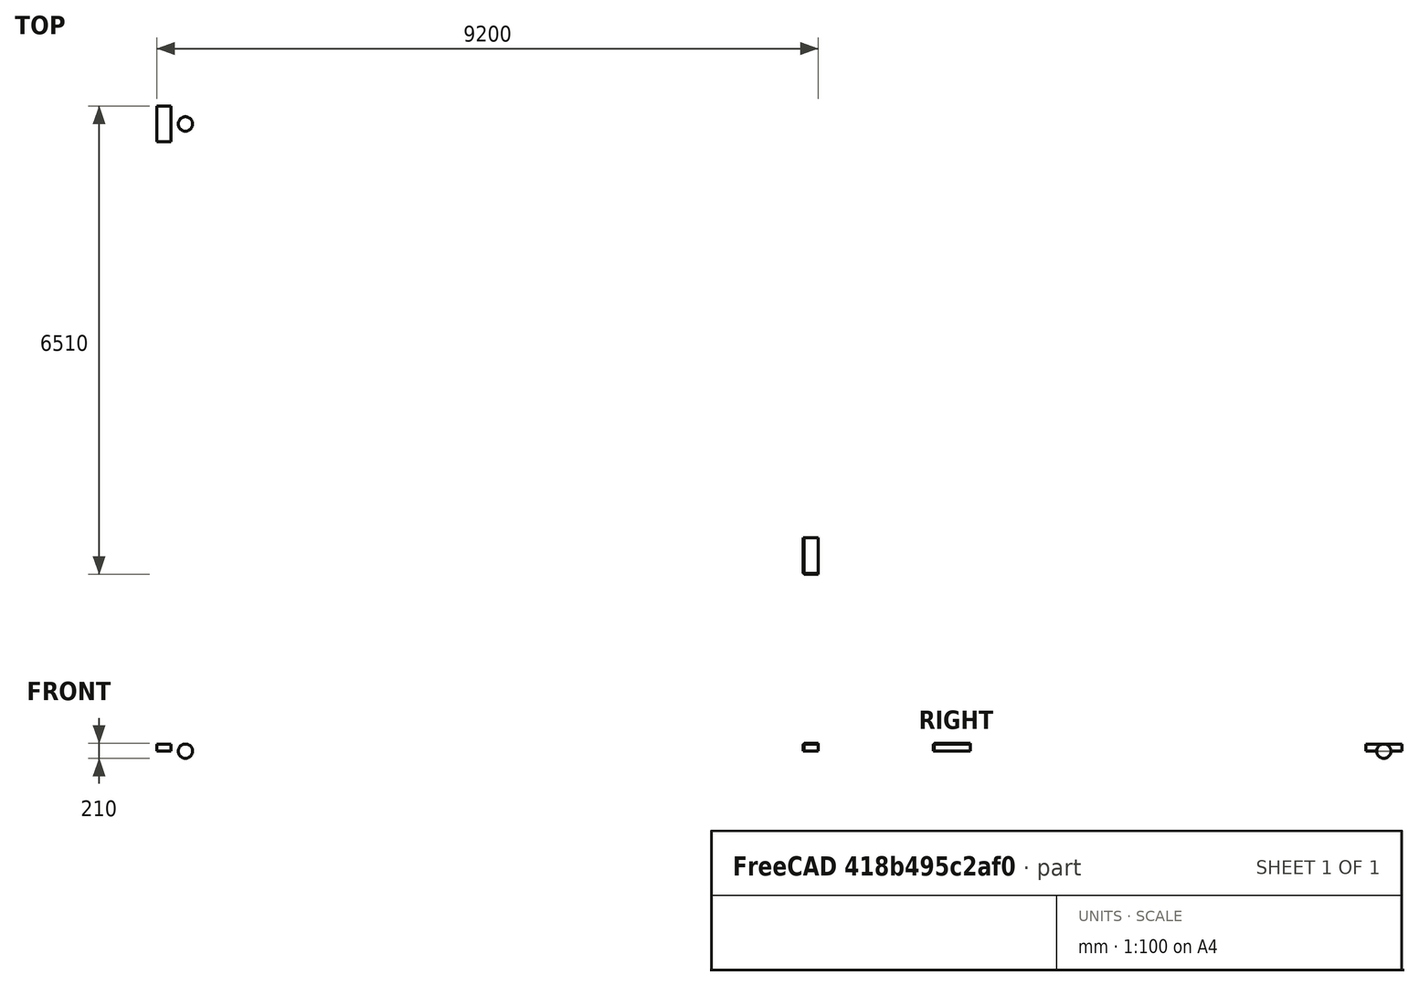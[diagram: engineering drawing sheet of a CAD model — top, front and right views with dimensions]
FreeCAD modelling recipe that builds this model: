
FCSTD DOCUMENT  (FreeCAD 0.20R28671 (Git))
Label: draft_test_objects
License: Creative Commons Attribution
LicenseURL: http://creativecommons.org/licenses/by/4.0/
objects: Part::Part2DObjectPython×39, App::Annotation×37, Part::FeaturePython×21, App::FeaturePython×9, Part::Box×3, Part::Feature×1, Part::Mirroring×1, Part::Sphere×1, App::DocumentObjectGroupPython×1
note: 62 computed .brp shape members not serialized (recipe doc carries the construction recipe); baked Part::Feature solids carry a one-line shape summary decoded from their .brp

FEATURE [App::Annotation] Description
  LabelText = Draft test file | Created: 2022/04/14T09:40:22 | Version: 0.20.28671 (Git) | Release: Unknown 2022/04/09 23:07:02 | Branch: 
  Position = (0,-1000,0)
FEATURE [Part::Feature] Frame
  shape: bbox 18000 x 12000 x 2e-07 mm, 0 faces, 0 solids (baked)
FEATURE [Part::Part2DObjectPython] Line  # Draft 2D object (typed FeaturePython)
  Area = 0
  ChamferSize = 0
  Closed = false
  End = (500,500,0)
  FilletRadius = 0
  Length = 707.107
  MakeFace = true
  Points = (2) [(0,0,0),(500,500,0)]
  Start = (0,0,0)
  Subdivisions = 0
FEATURE [App::Annotation] Annotation
  LabelText = Line
  Position = (0,-200,0)
FEATURE [Part::Part2DObjectPython] Wire  # Draft 2D object (typed FeaturePython)
  Area = 0
  ChamferSize = 0
  Closed = false
  End = (1500,500,0)
  FilletRadius = 0
  Length = 809.017
  MakeFace = true
  Points = (3) [(1000,0,0),(1500,250,0),(1500,500,0)]
  Start = (1000,0,0)
  Subdivisions = 0
FEATURE [App::Annotation] Annotation001
  LabelText = Wire
  Position = (1000,-200,0)
FEATURE [Part::Part2DObjectPython] Line001  # Draft 2D object (typed FeaturePython)
  Area = 0
  ChamferSize = 0
  Closed = false
  End = (2000,500,0)
  FilletRadius = 0
  Length = 500
  MakeFace = true
  Points = (2) [(2000,0,0),(2000,500,0)]
  Start = (2000,0,0)
  Subdivisions = 0
FEATURE [Part::Part2DObjectPython] Line002  # Draft 2D object (typed FeaturePython)
  Area = 0
  ChamferSize = 0
  Closed = false
  End = (2500,500,0)
  FilletRadius = 0
  Length = 500
  MakeFace = true
  Points = (2) [(2000,500,0),(2500,500,0)]
  Start = (2000,500,0)
  Subdivisions = 0
FEATURE [Part::Part2DObjectPython] Fillet  # Draft 2D object (typed FeaturePython)
  End = (2500,500,0)
  FilletRadius = 400
  Length = 828.319
  Start = (2000,0,0)
FEATURE [App::Annotation] Annotation002
  LabelText = Fillet
  Position = (2000,-200,0)
FEATURE [Part::Part2DObjectPython] Arc  # Draft 2D object (typed FeaturePython)
  Area = 0
  FirstAngle = 90
  LastAngle = 270
  MakeFace = true
  Placement = pos=(3250,250,0) rot=(0,0,1;0rad)
  Radius = 250
FEATURE [App::Annotation] Annotation003
  LabelText = Circular arc
  Position = (3000,-200,0)
FEATURE [Part::Part2DObjectPython] Arc001  # Draft 2D object (typed FeaturePython)
  Area = 0
  FirstAngle = 0
  LastAngle = 180
  MakeFace = false
  Placement = pos=(4250,250,0) rot=(0.707107,-0.707107,0;3.14159rad)
  Radius = 250
FEATURE [App::Annotation] Annotation004
  LabelText = Circular arc 3 points
  Position = (4000,-200,0)
FEATURE [Part::Part2DObjectPython] Circle  # Draft 2D object (typed FeaturePython)
  Area = 196350
  FirstAngle = 0
  LastAngle = 0
  MakeFace = true
  Placement = pos=(5250,250,0) rot=(0,0,1;0rad)
  Radius = 250
FEATURE [App::Annotation] Annotation005
  LabelText = Circle
  Position = (5000,-200,0)
FEATURE [Part::Part2DObjectPython] Ellipse  # Draft 2D object (typed FeaturePython)
  Area = 117810
  FirstAngle = 0
  LastAngle = 0
  MajorRadius = 250
  MakeFace = true
  MinorRadius = 150
  Placement = pos=(6250,150,0) rot=(0,0,1;0rad)
FEATURE [App::Annotation] Annotation006
  LabelText = Ellipse
  Position = (6000,-200,0)
FEATURE [Part::Part2DObjectPython] Rectangle  # Draft 2D object (typed FeaturePython)
  Area = 150000
  ChamferSize = 0
  Columns = 1
  FilletRadius = 0
  Height = 300
  Length = 500
  MakeFace = true
  Placement = pos=(7000,0,0) rot=(0,0,1;0rad)
  Rows = 1
FEATURE [App::Annotation] Annotation007
  LabelText = Rectangle
  Position = (7000,-200,0)
FEATURE [Part::Part2DObjectPython] Polygon  # Draft 2D object (typed FeaturePython)
  Area = 148603
  ChamferSize = 0
  DrawMode = 0
  FacesNumber = 5
  FilletRadius = 0
  MakeFace = true
  Placement = pos=(8250,250,0) rot=(0,0,1;0rad)
  Radius = 250
FEATURE [App::Annotation] Annotation008
  LabelText = Polygon
  Position = (8000,-200,0)
FEATURE [Part::Part2DObjectPython] BSpline  # Draft 2D object (typed FeaturePython)
  Area = 0
  Closed = false
  MakeFace = true
  Parameterization = 1
  Points = (4) [(9000,0,0),(9100,200,0),(9400,300,0),(9500,500,0)]
FEATURE [App::Annotation] Annotation009
  LabelText = BSpline
  Position = (9000,-200,0)
FEATURE [Part::Part2DObjectPython] BezCurve  # Draft 2D object (typed FeaturePython)
  Area = 0
  Closed = false
  Degree = 3
  Length = 838.374
  MakeFace = true
  Points = (4) [(10000,0,0),(10000,500,0),(10500,0,0),(10500,500,0)]
FEATURE [App::Annotation] Annotation010
  LabelText = Cubic bezier
  Position = (10000,-200,0)
FEATURE [Part::Part2DObjectPython] BezCurve001  # Draft 2D object (typed FeaturePython)
  Area = 0
  Closed = false
  Degree = 4
  Length = 800.125
  MakeFace = true
  Points = (5) [(11000,0,0),(11100,400,0),(11250,250,0),(11400,100,0),(11500,500,0)]
FEATURE [App::Annotation] Annotation011
  LabelText = N-degree bezier
  Position = (11000,-200,0)
FEATURE [Part::FeaturePython] Point  # WARN: FeaturePython — macro-defined, semantics opaque (R4)
  Placement = pos=(12000,0,0) rot=(0,0,1;0rad)
  X = 12000
  Y = 0
  Z = 0
FEATURE [App::Annotation] Annotation012
  LabelText = Point
  Position = (12000,-200,0)
FEATURE [Part::Box] Box
  AttacherType = Attacher::AttachEngine3D
  Height = 100
  Length = 200
  Placement = pos=(13000,0,0) rot=(0,0,1;0rad)
  Width = 500
FEATURE [Part::FeaturePython] Facebinder  # WARN: FeaturePython — macro-defined, semantics opaque (R4)
  Area = 170000
  Extrusion = 10
  Faces = -> [Box]
  RemoveSplitter = false
  Sew = false
FEATURE [App::Annotation] Annotation013
  LabelText = Facebinder
  Position = (13000,-200,0)
FEATURE [Part::Part2DObjectPython] ShapeString  # Draft 2D object (typed FeaturePython)
  FontFile = <path>
  MakeFace = true
  Placement = pos=(14000,0,0) rot=(0,0,1;0rad)
  Size = 100
  String = Testing
  Tracking = 0
FEATURE [App::Annotation] Annotation014
  LabelText = Shapestring
  Position = (14000,-200,0)
FEATURE [Part::Part2DObjectPython] Rectangle001  # Draft 2D object (typed FeaturePython)
  Area = 150000
  ChamferSize = 0
  Columns = 1
  FilletRadius = 0
  Height = 300
  Length = 500
  MakeFace = true
  Placement = pos=(15000,0,0) rot=(0,0,1;0rad)
  Rows = 1
FEATURE [Part::FeaturePython] Hatch  # WARN: FeaturePython — macro-defined, semantics opaque (R4)
  Base = -> Rectangle001
  File = <path>
  Pattern = Horizontal5
  Rotation = 45
  Scale = 10
  Translate = true
FEATURE [App::Annotation] Annotation015
  LabelText = Hatch
  Position = (15000,-200,0)
FEATURE [App::FeaturePython] Text  # WARN: FeaturePython — macro-defined, semantics opaque (R4)
  Placement = pos=(0,2100,0) rot=(0,0,1;0rad)
  Text = Testing | text
FEATURE [App::Annotation] Annotation016
  LabelText = Text
  Position = (0,1800,0)
FEATURE [App::FeaturePython] Dimension  # Draft dimension (typed FeaturePython)
  Diameter = false
  Dimline = (1000,2200,0)
  Direction = (0,0,0)
  Distance = 400
  End = (1500,2400,0)
  Normal = (0,0,1)
  Start = (1500,2000,0)
FEATURE [Part::Part2DObjectPython] Line003  # Draft 2D object (typed FeaturePython)
  Area = 0
  ChamferSize = 0
  Closed = false
  End = (1500,3000,0)
  FilletRadius = 0
  Length = 400
  MakeFace = true
  Points = (2) [(1500,2600,0),(1500,3000,0)]
  Start = (1500,2600,0)
  Subdivisions = 0
FEATURE [App::FeaturePython] Dimension001  # Draft dimension (typed FeaturePython)
  Diameter = false
  Dimline = (1000,2800,0)
  Direction = (0,0,0)
  Distance = 400
  End = (1500,3000,0)
  LinkedGeometry = -> [Line003]
  Normal = (0,0,1)
  Start = (1500,2600,0)
  Support = -> Line003
FEATURE [App::Annotation] Annotation017
  LabelText = Dimension
  Position = (1000,1800,0)
FEATURE [Part::Part2DObjectPython] Circle001  # Draft 2D object (typed FeaturePython)
  Area = 0
  FirstAngle = 0
  LastAngle = 0
  MakeFace = false
  Placement = pos=(2200,2200,0) rot=(0,0,1;0rad)
  Radius = 200
FEATURE [App::FeaturePython] Dimension002  # Draft dimension (typed FeaturePython)
  Diameter = false
  Dimline = (2300,2300,0)
  Direction = (0,0,0)
  Distance = 200
  End = (2341.42,2341.42,0)
  LinkedGeometry = -> [Circle001]
  Normal = (0,0,1)
  Start = (2200,2200,0)
  Support = -> Circle001
FEATURE [Part::Part2DObjectPython] Circle002  # Draft 2D object (typed FeaturePython)
  Area = 0
  FirstAngle = 0
  LastAngle = 0
  MakeFace = false
  Placement = pos=(2200,2800,0) rot=(0,0,1;0rad)
  Radius = 200
FEATURE [App::FeaturePython] Dimension003  # Draft dimension (typed FeaturePython)
  Diameter = true
  Dimline = (2300,2900,0)
  Direction = (0,0,0)
  Distance = 400
  End = (2341.42,2941.42,0)
  LinkedGeometry = -> [Circle002]
  Normal = (0,0,1)
  Start = (2058.58,2658.58,0)
  Support = -> Circle002
FEATURE [App::Annotation] Annotation018
  LabelText = Radius dimension | Diameter dimension
  Position = (2000,1800,0)
FEATURE [Part::Part2DObjectPython] Line004  # Draft 2D object (typed FeaturePython)
  Area = 0
  ChamferSize = 0
  Closed = false
  End = (3500,2000,0)
  FilletRadius = 0
  Length = 500
  MakeFace = true
  Points = (2) [(3000,2000,0),(3500,2000,0)]
  Start = (3000,2000,0)
  Subdivisions = 0
FEATURE [Part::Part2DObjectPython] Line005  # Draft 2D object (typed FeaturePython)
  Area = 0
  ChamferSize = 0
  Closed = false
  End = (3500,2500,0)
  FilletRadius = 0
  Length = 707.107
  MakeFace = true
  Points = (2) [(3000,2000,0),(3500,2500,0)]
  Start = (3000,2000,0)
  Subdivisions = 0
FEATURE [App::FeaturePython] Dimension004  # Draft dimension (typed FeaturePython)
  Angle = 45
  Center = (3000,2000,0)
  Dimline = (3250,2250,0)
  FirstAngle = 0
  LastAngle = 45
  Normal = (0,0,1)
FEATURE [App::Annotation] Annotation019
  LabelText = Angle dimension
  Position = (3000,1800,0)
FEATURE [App::FeaturePython] dLabel  # WARN: FeaturePython — macro-defined, semantics opaque (R4)
  CustomText = Example label
  LabelType = 0
  Placement = pos=(4250,2250,0) rot=(0,0,1;0rad)
  Points = (3) [(4250,2250,0),(4150,2250,0),(4000,2000,0)]
  StraightDirection = 0
  StraightDistance = -100
  TargetPoint = (4000,2000,0)
  Text = Example label
FEATURE [App::Annotation] Annotation020
  LabelText = Label
  Position = (4000,1800,0)
FEATURE [Part::Part2DObjectPython] Rectangle002  # Draft 2D object (typed FeaturePython)
  Area = 5000
  ChamferSize = 0
  Columns = 1
  FilletRadius = 0
  Height = 50
  Length = 100
  MakeFace = true
  Placement = pos=(0,4000,0) rot=(0,0,1;0rad)
  Rows = 1
FEATURE [Part::FeaturePython] Array  # Draft array (typed FeaturePython)
  Angle = 360
  ArrayType = 0
  Axis = (0,0,1)
  Base = -> Rectangle002
  Center = (0,0,0)
  Fuse = false
  IntervalAxis = (0,0,0)
  IntervalX = (200,0,0)
  IntervalY = (0,150,0)
  IntervalZ = (0,0,0)
  NumberCircles = 3
  NumberPolar = 5
  NumberX = 3
  NumberY = 2
  NumberZ = 1
  RadialDistance = 50
  Symmetry = 1
  TangentialDistance = 25
FEATURE [App::Annotation] Annotation021
  LabelText = Orthogonal array
  Position = (0,3800,0)
FEATURE [Part::Part2DObjectPython] Rectangle003  # Draft 2D object (typed FeaturePython)
  Area = 2500
  ChamferSize = 0
  Columns = 1
  FilletRadius = 0
  Height = 50
  Length = 50
  MakeFace = true
  Placement = pos=(1000,4000,0) rot=(0,0,1;0rad)
  Rows = 1
FEATURE [Part::FeaturePython] Array001  # Draft array (typed FeaturePython)
  AlwaysSyncPlacement = false
  Angle = 360
  ArrayType = 0
  Axis = (0,0,1)
  Base = -> Rectangle003
  Center = (0,0,0)
  Count = 6
  ExpandArray = false
  Fuse = false
  IntervalAxis = (0,0,0)
  IntervalX = (200,0,0)
  IntervalY = (0,150,0)
  IntervalZ = (0,0,0)
  NumberCircles = 3
  NumberPolar = 5
  NumberX = 3
  NumberY = 2
  NumberZ = 1
  PlacementList = 6 placements: [(1000,4000,0),(1000,4150,0),(1200,4000,0),(1200,4150,0),(1400,4000,0),(1400,4150,0)]
  RadialDistance = 50
  ScaleList = (6) [(1,1,1),(1,1,1),(1,1,1),(1,1,1),(1,1,1),(1,1,1)]
  Symmetry = 1
  TangentialDistance = 25
FEATURE [App::Annotation] Annotation022
  LabelText = Orthogonal link array
  Position = (1000,3800,0)
FEATURE [Part::Part2DObjectPython] Wire001  # Draft 2D object (typed FeaturePython)
  Area = 0
  ChamferSize = 0
  Closed = false
  End = (2100,4000,0)
  FilletRadius = 0
  Length = 150
  MakeFace = true
  Points = (3) [(2000,4050,0),(2000,4000,0),(2100,4000,0)]
  Start = (2000,4050,0)
  Subdivisions = 0
FEATURE [Part::FeaturePython] Array002  # Draft array (typed FeaturePython)
  Angle = 90
  ArrayType = 1
  Axis = (0,0,1)
  Base = -> Wire001
  Center = (2000,4250,0)
  Fuse = false
  IntervalAxis = (0,0,0)
  IntervalX = (50,0,0)
  IntervalY = (0,50,0)
  IntervalZ = (0,0,50)
  NumberCircles = 3
  NumberPolar = 4
  NumberX = 2
  NumberY = 2
  NumberZ = 1
  RadialDistance = 50
  Symmetry = 1
  TangentialDistance = 25
FEATURE [App::Annotation] Annotation023
  LabelText = Polar array
  Position = (2000,3800,0)
FEATURE [Part::Part2DObjectPython] Wire002  # Draft 2D object (typed FeaturePython)
  Area = 0
  ChamferSize = 0
  Closed = false
  End = (3050,4000,0)
  FilletRadius = 0
  Length = 100
  MakeFace = true
  Points = (3) [(3000,4050,0),(3000,4000,0),(3050,4000,0)]
  Start = (3000,4050,0)
  Subdivisions = 0
FEATURE [Part::FeaturePython] Array003  # Draft array (typed FeaturePython)
  AlwaysSyncPlacement = false
  Angle = 90
  ArrayType = 1
  Axis = (0,0,1)
  Base = -> Wire002
  Center = (3000,4250,0)
  Count = 4
  ExpandArray = false
  Fuse = false
  IntervalAxis = (0,0,0)
  IntervalX = (50,0,0)
  IntervalY = (0,50,0)
  IntervalZ = (0,0,50)
  NumberCircles = 3
  NumberPolar = 4
  NumberX = 2
  NumberY = 2
  NumberZ = 1
  PlacementList = 4 placements: [(0,0,0),(2526.92,-930.608,0),(5180.61,-473.076,0),(7250,1250,0)]
  RadialDistance = 50
  ScaleList = (4) [(1,1,1),(1,1,1),(1,1,1),(1,1,1)]
  Symmetry = 1
  TangentialDistance = 25
FEATURE [App::Annotation] Annotation024
  LabelText = Polar link array
  Position = (3000,3800,0)
FEATURE [Part::Part2DObjectPython] Polygon001  # Draft 2D object (typed FeaturePython)
  Area = 2139.88
  ChamferSize = 0
  DrawMode = 0
  FacesNumber = 5
  FilletRadius = 0
  MakeFace = true
  Placement = pos=(4250,4250,0) rot=(0,0,1;0rad)
  Radius = 30
FEATURE [Part::FeaturePython] Array004  # Draft array (typed FeaturePython)
  Angle = 360
  ArrayType = 2
  Axis = (0,0,1)
  Base = -> Polygon001
  Center = (0,0,0)
  Fuse = false
  IntervalAxis = (0,0,0)
  IntervalX = (50,0,0)
  IntervalY = (0,50,0)
  IntervalZ = (0,0,50)
  NumberCircles = 3
  NumberPolar = 5
  NumberX = 2
  NumberY = 2
  NumberZ = 1
  RadialDistance = 110
  Symmetry = 1
  TangentialDistance = 100
FEATURE [App::Annotation] Annotation025
  LabelText = Circular array
  Position = (4000,3800,0)
FEATURE [Part::Part2DObjectPython] Polygon002  # Draft 2D object (typed FeaturePython)
  Area = 2338.27
  ChamferSize = 0
  DrawMode = 0
  FacesNumber = 6
  FilletRadius = 0
  MakeFace = true
  Placement = pos=(5250,4250,0) rot=(0,0,1;0rad)
  Radius = 30
FEATURE [Part::FeaturePython] Array005  # Draft array (typed FeaturePython)
  AlwaysSyncPlacement = false
  Angle = 360
  ArrayType = 2
  Axis = (0,0,1)
  Base = -> Polygon002
  Center = (0,0,0)
  Count = 20
  ExpandArray = false
  Fuse = false
  IntervalAxis = (0,0,0)
  IntervalX = (50,0,0)
  IntervalY = (0,50,0)
  IntervalZ = (0,0,50)
  NumberCircles = 3
  NumberPolar = 5
  NumberX = 2
  NumberY = 2
  NumberZ = 1
  PlacementList = 20 placements: [(5250,4250,0),(5140,4250,0),(5195,4154.74,0),(5305,4154.74,0),(5360,4250,0),(5305,4345.26,0),(5195,4345.26,0),(5030,4250,0),(5055.2,4147.76,0),(5125.03,4068.94,0),(5223.48,4031.6,0),(5328.01,4044.3,0),(5414.67,4104.11,0),(5463.61,4197.35,0),(5463.61,4302.65,0),(5414.67,4395.89,0),(5328.01,4455.7,0),(5223.48,4468.4,0),(5125.03,4431.06,0),(5055.2,4352.24,0)]
  RadialDistance = 110
  ScaleList = (20) [(1,1,1),(1,1,1),(1,1,1),(1,1,1),(1,1,1),(1,1,1),(1,1,1),(1,1,1),(1,1,1),(1,1,1),(1,1,1),(1,1,1),(1,1,1),(1,1,1),(1,1,1),(1,1,1),(1,1,1),(1,1,1),(1,1,1),(1,1,1)]
  Symmetry = 1
  TangentialDistance = 100
FEATURE [App::Annotation] Annotation026
  LabelText = Circular link array
  Position = (5000,3800,0)
FEATURE [Part::Part2DObjectPython] Polygon003  # Draft 2D object (typed FeaturePython)
  Area = 1169.13
  ChamferSize = 0
  DrawMode = 0
  FacesNumber = 3
  FilletRadius = 0
  MakeFace = true
  Placement = pos=(6000,4000,0) rot=(0,0,1;0rad)
  Radius = 30
FEATURE [Part::Part2DObjectPython] BSpline001  # Draft 2D object (typed FeaturePython)
  Area = 0
  Closed = false
  MakeFace = true
  Parameterization = 1
  Points = (4) [(6000,4000,0),(6100,4200,0),(6400,4300,0),(6500,4500,0)]
FEATURE [Part::FeaturePython] PathArray  # WARN: FeaturePython — macro-defined, semantics opaque (R4)
  Align = false
  AlignMode = 0
  Base = -> Polygon003
  Count = 5
  ExtraTranslation = (0,0,0)
  ForceVertical = false
  PathObject = -> BSpline001
  TangentVector = (1,0,0)
  VerticalVector = (0,0,1)
FEATURE [App::Annotation] Annotation027
  LabelText = Path array
  Position = (6000,3800,0)
FEATURE [Part::Part2DObjectPython] Polygon004  # Draft 2D object (typed FeaturePython)
  Area = 1800
  ChamferSize = 0
  DrawMode = 0
  FacesNumber = 4
  FilletRadius = 0
  MakeFace = true
  Placement = pos=(7000,4000,0) rot=(0,0,1;0rad)
  Radius = 30
FEATURE [Part::Part2DObjectPython] BSpline002  # Draft 2D object (typed FeaturePython)
  Area = 0
  Closed = false
  MakeFace = true
  Parameterization = 1
  Points = (4) [(7000,4000,0),(7100,4200,0),(7400,4300,0),(7500,4500,0)]
FEATURE [Part::FeaturePython] PathArray001  # WARN: FeaturePython — macro-defined, semantics opaque (R4)
  Align = false
  AlignMode = 0
  AlwaysSyncPlacement = false
  Base = -> Polygon004
  Count = 5
  ExpandArray = false
  ExtraTranslation = (0,0,0)
  ForceVertical = false
  PathObject = -> BSpline002
  PlacementList = 5 placements: [(7000,4000,0),(7500,4500,0),(7067.31,4178.13,0),(7250,4250,0),(7432.69,4321.87,0)]
  ScaleList = (5) [(1,1,1),(1,1,1),(1,1,1),(1,1,1),(1,1,1)]
  TangentVector = (1,0,0)
  VerticalVector = (0,0,1)
FEATURE [App::Annotation] Annotation028
  LabelText = Path link array
  Position = (7000,3800,0)
FEATURE [Part::Part2DObjectPython] Polygon005  # Draft 2D object (typed FeaturePython)
  Area = 1169.13
  ChamferSize = 0
  DrawMode = 0
  FacesNumber = 3
  FilletRadius = 0
  MakeFace = true
  Placement = pos=(8000,4000,0) rot=(0,0,1;0rad)
  Radius = 30
FEATURE [Part::FeaturePython] Point001  # WARN: FeaturePython — macro-defined, semantics opaque (R4)
  Placement = pos=(8030,4030,0) rot=(0,0,1;0rad)
  X = 8030
  Y = 4030
  Z = 0
FEATURE [Part::FeaturePython] Point002  # WARN: FeaturePython — macro-defined, semantics opaque (R4)
  Placement = pos=(8030,4250,0) rot=(0,0,1;0rad)
  X = 8030
  Y = 4250
  Z = 0
FEATURE [Part::FeaturePython] Point003  # WARN: FeaturePython — macro-defined, semantics opaque (R4)
  Placement = pos=(8470,4250,0) rot=(0,0,1;0rad)
  X = 8470
  Y = 4250
  Z = 0
FEATURE [Part::FeaturePython] Point004  # WARN: FeaturePython — macro-defined, semantics opaque (R4)
  Placement = pos=(8470,4470,0) rot=(0,0,1;0rad)
  X = 8470
  Y = 4470
  Z = 0
FEATURE [Part::Part2DObjectPython] Block  # Draft 2D object (typed FeaturePython)
  Components = -> [Point001,Point002,Point003,Point004]
FEATURE [Part::FeaturePython] PointArray  # Draft array (typed FeaturePython)
  Base = -> Polygon005
  Count = 4
  PointObject = -> Block
FEATURE [App::Annotation] Annotation029
  LabelText = Point array
  Position = (8000,3800,0)
FEATURE [Part::Part2DObjectPython] Polygon006  # Draft 2D object (typed FeaturePython)
  Area = 1800
  ChamferSize = 0
  DrawMode = 0
  FacesNumber = 4
  FilletRadius = 0
  MakeFace = true
  Placement = pos=(9000,4000,0) rot=(0,0,1;0rad)
  Radius = 30
FEATURE [Part::FeaturePython] Point005  # WARN: FeaturePython — macro-defined, semantics opaque (R4)
  Placement = pos=(9030,4030,0) rot=(0,0,1;0rad)
  X = 9030
  Y = 4030
  Z = 0
FEATURE [Part::FeaturePython] Point006  # WARN: FeaturePython — macro-defined, semantics opaque (R4)
  Placement = pos=(9030,4250,0) rot=(0,0,1;0rad)
  X = 9030
  Y = 4250
  Z = 0
FEATURE [Part::FeaturePython] Point007  # WARN: FeaturePython — macro-defined, semantics opaque (R4)
  Placement = pos=(9470,4250,0) rot=(0,0,1;0rad)
  X = 9470
  Y = 4250
  Z = 0
FEATURE [Part::FeaturePython] Point008  # WARN: FeaturePython — macro-defined, semantics opaque (R4)
  Placement = pos=(9470,4470,0) rot=(0,0,1;0rad)
  X = 9470
  Y = 4470
  Z = 0
FEATURE [Part::Part2DObjectPython] Block001  # Draft 2D object (typed FeaturePython)
  Components = -> [Point005,Point006,Point007,Point008]
FEATURE [Part::FeaturePython] PointArray001  # Draft array (typed FeaturePython)
  AlwaysSyncPlacement = false
  Base = -> Polygon006
  Count = 4
  ExpandArray = false
  PlacementList = 4 placements: [(9030,4030,0),(9030,4250,0),(9470,4250,0),(9470,4470,0)]
  PointObject = -> Block001
  ScaleList = (4) [(1,1,1),(1,1,1),(1,1,1),(1,1,1)]
FEATURE [App::Annotation] Annotation030
  LabelText = Point link array
  Position = (9000,3800,0)
FEATURE [Part::Part2DObjectPython] Wire003  # Draft 2D object (typed FeaturePython)
  Area = 0
  ChamferSize = 0
  Closed = false
  End = (500,6000,0)
  FilletRadius = 0
  Length = 653.113
  MakeFace = true
  Points = (3) [(0,6000,0),(150,6200,0),(500,6000,0)]
  Start = (0,6000,0)
  Subdivisions = 0
FEATURE [Part::Mirroring] mirror  label="Wire003 (mirrored) "
  Base = (0,6250,0)
  Normal = (0,-1,0)
  Source = -> Wire003
FEATURE [App::Annotation] Annotation031
  LabelText = Mirror
  Position = (0,5800,0)
FEATURE [Part::Part2DObjectPython] Wire004  # Draft 2D object (typed FeaturePython)
  Area = 0
  ChamferSize = 0
  Closed = false
  End = (1500,6000,0)
  FilletRadius = 0
  Length = 653.113
  MakeFace = true
  Points = (3) [(1000,6000,0),(1150,6200,0),(1500,6000,0)]
  Start = (1000,6000,0)
  Subdivisions = 0
FEATURE [Part::Part2DObjectPython] Clone2D  label="Wire004 (2D)"  # Draft 2D object (typed FeaturePython)
  Fuse = false
  Objects = -> [Wire004]
  Placement = pos=(0,300,0) rot=(0,0,1;0rad)
  Scale = (1,1,1)
FEATURE [App::Annotation] Annotation032
  LabelText = Clone
  Position = (1000,5800,0)
FEATURE [Part::Box] Box001
  AttacherType = Attacher::AttachEngine3D
  Height = 100
  Length = 200
  Placement = pos=(2000,6000,0) rot=(-0.894427,0.447214,0;0.640522rad)
  Width = 500
FEATURE [Part::Part2DObjectPython] Shape2DView  # Draft 2D object (typed FeaturePython)
  AutoUpdate = true
  Base = -> Box001
  Clip = false
  FuseArch = false
  HiddenLines = false
  InPlace = true
  OnlySolids = false
  Projection = (0,0,1)
  ProjectionMode = 0
  SegmentLength = 0.05
  Tessellation = false
  VisibleOnly = false
FEATURE [App::Annotation] Annotation033
  LabelText = Shape2DView
  Position = (2000,5800,0)
FEATURE [App::FeaturePython] WPProxy  # WARN: FeaturePython — macro-defined, semantics opaque (R4)
  Placement = pos=(3250,6250,0) rot=(0,0,1;0rad)
FEATURE [App::Annotation] Annotation034
  LabelText = WorkingPlaneProxy
  Position = (3000,5800,0)
FEATURE [Part::Box] Box002
  AttacherType = Attacher::AttachEngine3D
  Height = 100
  Length = 200
  Placement = pos=(4000,6000,0) rot=(0,0,1;0rad)
  Width = 500
FEATURE [Part::Sphere] Sphere
  Angle1 = -90
  Angle2 = 90
  Angle3 = 360
  AttacherType = Attacher::AttachEngine3D
  Placement = pos=(4400,6250,0) rot=(0,0,1;0rad)
  Radius = 100
FEATURE [App::FeaturePython] Layer  label="Custom layer"  # WARN: FeaturePython — macro-defined, semantics opaque (R4)
  Group = -> [Box002,Sphere]
FEATURE [App::DocumentObjectGroupPython] LayerContainer  label="Layers"  # scripted group (container) (typed FeaturePython)
  Group = -> [Layer]
FEATURE [App::Annotation] Annotation035
  LabelText = Layer
  Position = (4000,5800,0)
note: 2 file-system paths scrubbed to <path> (originals preserved in the JSON sidecar)
